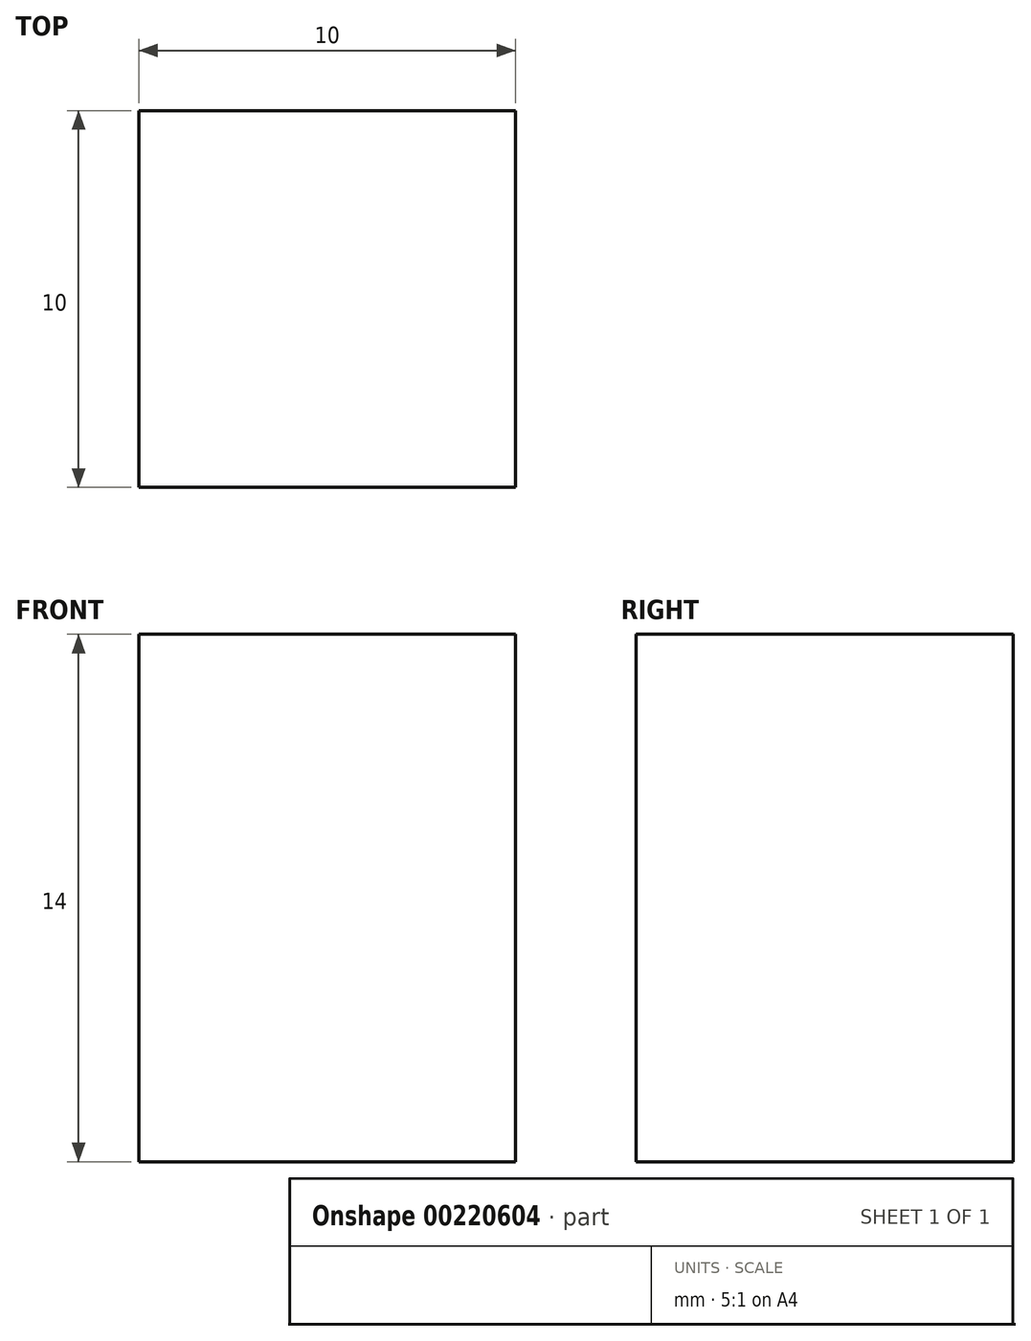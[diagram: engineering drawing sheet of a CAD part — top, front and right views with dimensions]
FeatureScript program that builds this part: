
annotation { "Feature Type Name" : "Feature", "Feature Type Description" : "" }
export const myFeature = defineFeature(function(context is Context, id is Id, definition is map)
    precondition{}
    {
        {
            var Q0;
            Q0=qCreatedBy(makeId("Top.planeOp"),FACE);
            var sketch = newSketch(context, id + "F0", { "sketchPlane" : qUnion([Q0])});
            skLineSegment(sketch, "E0.bottom", {"start": v(0, 0) * mm, "end": v(70, 0) * mm});
            skLineSegment(sketch, "E0.top", {"start": v(0, 50) * mm, "end": v(70, 50) * mm});
            skLineSegment(sketch, "E0.left", {"start": v(0, 0) * mm, "end": v(0, 50) * mm});
            skLineSegment(sketch, "E0.right", {"start": v(70, 0) * mm, "end": v(70, 50) * mm});
            skLineSegment(sketch, "E1.bottom", {"start": v(0, 0) * mm, "end": v(10, 0) * mm});
            skLineSegment(sketch, "E1.top", {"start": v(0, 10) * mm, "end": v(10, 10) * mm});
            skLineSegment(sketch, "E1.left", {"start": v(0, 0) * mm, "end": v(0, 10) * mm});
            skLineSegment(sketch, "E1.right", {"start": v(10, 0) * mm, "end": v(10, 10) * mm});
            skSolve(sketch);
        }
        {
            var Q0;
            Q0=makeQuery(id+"F0.imprint","IMPRINT",FACE,{"disambiguationData":[TD([[makeQuery(id+"F0.imprint","IMPRINT",EDGE,{"derivedFrom":sQuery(id+"F0.wireOp",EDGE,"E0.bottom")}),1.0]])]});
            extrude(context, id + "F1", {"entities" : qUnion([Q0]), "depth" : 14 * mm});
        }
        {
            var Q0;
            Q0=makeQuery(id+"F1.opExtrude","CAP_FACE",FACE,{"disambiguationData":[OSD([sQuery(id+"F0.wireOp",EDGE,"E0.bottom"),sQuery(id+"F0.wireOp",EDGE,"E0.top"),sQuery(id+"F0.wireOp",EDGE,"E0.left"),sQuery(id+"F0.wireOp",EDGE,"E0.right"),sQuery(id+"F0.wireOp",EDGE,"E1.top"),sQuery(id+"F0.wireOp",EDGE,"E1.right")])],"isStart":false});
            var sketch = newSketch(context, id + "F2", { "sketchPlane" : qUnion([Q0])});
            skCircle(sketch, "E2", {"center": v(29, 25) * mm, "radius": 19.25 * mm});
            skCircle(sketch, "E3", {"center": v(60, 35) * mm, "radius": 2.62 * mm});
            skLineSegment(sketch, "E4", {"start": v(70, 25) * mm, "end": v(0, 25) * mm, "construction": true});
            skCircle(sketch, "E5.MirrorC", {"center": v(60, 15) * mm, "radius": 2.62 * mm});
            skLineSegment(sketch, "E6.bottom", {"start": v(0, 50) * mm, "end": v(10, 50) * mm});
            skLineSegment(sketch, "E6.top", {"start": v(0, 40) * mm, "end": v(10, 40) * mm});
            skLineSegment(sketch, "E6.left", {"start": v(0, 50) * mm, "end": v(0, 40) * mm});
            skLineSegment(sketch, "E6.right", {"start": v(10, 50) * mm, "end": v(10, 40) * mm});
            skSolve(sketch);
        }
        {
            var Q0;
            Q0=makeQuery(id+"F2.imprint","IMPRINT",FACE,{"disambiguationData":[TD([[makeQuery(id+"F2.imprint","IMPRINT",EDGE,{"derivedFrom":sQuery(id+"F2.wireOp",EDGE,"E2")}),1.0]])]});
            var Q1;
            Q1=makeQuery(id+"F2.imprint","IMPRINT",FACE,{"disambiguationData":[TD([[makeQuery(id+"F2.imprint","IMPRINT",EDGE,{"derivedFrom":sQuery(id+"F2.wireOp",EDGE,"E3")}),1.0]])]});
            var Q2;
            Q2=makeQuery(id+"F2.imprint","IMPRINT",FACE,{"disambiguationData":[TD([[makeQuery(id+"F2.imprint","IMPRINT",EDGE,{"derivedFrom":sQuery(id+"F2.wireOp",EDGE,"E5.MirrorC")}),-1.0]])]});
            var Q3;
            Q3=makeQuery(id+"F2.imprint","IMPRINT",FACE,{"disambiguationData":[TD([[makeQuery(id+"F2.imprint","IMPRINT",EDGE,{"derivedFrom":sQuery(id+"F2.wireOp",EDGE,"E6.bottom")}),-1.0]])]});
            extrude(context, id + "F3", {"entities" : qUnion([Q0, Q1, Q2, Q3]), "operationType" : NewBodyOperationType.REMOVE, "oppositeDirection" : true, "depth" : 25 * mm});
        }
        {
            var Q0;
            Q0=makeQuery(id+"F1.opExtrude","CAP_FACE",FACE,{"disambiguationData":[OSD([sQuery(id+"F0.wireOp",EDGE,"E0.bottom"),sQuery(id+"F0.wireOp",EDGE,"E0.top"),sQuery(id+"F0.wireOp",EDGE,"E0.left"),sQuery(id+"F0.wireOp",EDGE,"E0.right"),sQuery(id+"F0.wireOp",EDGE,"E1.top"),sQuery(id+"F0.wireOp",EDGE,"E1.right")])],"isStart":false});
            var sketch = newSketch(context, id + "F4", { "sketchPlane" : qUnion([Q0])});
            skLineSegment(sketch, "E7.bottom", {"start": v(0, 23.5) * mm, "end": v(13.62, 23.5) * mm});
            skLineSegment(sketch, "E7.top", {"start": v(0, 26.5) * mm, "end": v(13.62, 26.5) * mm});
            skLineSegment(sketch, "E7.left", {"start": v(0, 23.5) * mm, "end": v(0, 26.5) * mm});
            skLineSegment(sketch, "E7.right", {"start": v(13.62, 23.5) * mm, "end": v(13.62, 26.5) * mm});
            skSolve(sketch);
        }
        {
            var Q0;
            {var subQ0=sQuery(id+"F4.wireOp",EDGE,"E7.left");Q0=makeQuery(id+"F4.imprint","IMPRINT",FACE,{"disambiguationData":[TD([[makeQuery(id+"F4.imprint","IMPRINT",EDGE,{"derivedFrom":subQ0}),-1.0]])]});}
            extrude(context, id + "F5", {"entities" : qUnion([Q0]), "operationType" : NewBodyOperationType.REMOVE, "oppositeDirection" : true, "depth" : 25 * mm});
        }
        {
            var Q0;
            Q0=makeQuery(id+"F1.opExtrude","SWEPT_FACE",FACE,{"disambiguationData":[OSD([sQuery(id+"F0.wireOp",EDGE,"E1.top")])]});
            var sketch = newSketch(context, id + "F6", { "sketchPlane" : qUnion([Q0])});
            skLineSegment(sketch, "E8", {"start": v(5, 14) * mm, "end": v(5, 0) * mm, "construction": true});
            skLineSegment(sketch, "E9", {"start": v(0, 7) * mm, "end": v(10, 7) * mm, "construction": true});
            skCircle(sketch, "E10", {"center": v(5, 7) * mm, "radius": 2.62 * mm});
            skSolve(sketch);
        }
        {
            var Q0;
            Q0=makeQuery(id+"F6.imprint","IMPRINT",FACE,{"disambiguationData":[TD([[makeQuery(id+"F6.imprint","IMPRINT",EDGE,{"derivedFrom":sQuery(id+"F6.wireOp",EDGE,"E10")}),1.0]])]});
            extrude(context, id + "F7", {"entities" : qUnion([Q0]), "operationType" : NewBodyOperationType.REMOVE, "endBound" : BoundingType.THROUGH_ALL, "oppositeDirection" : true, "depth" : 25 * mm});
        }
    });
